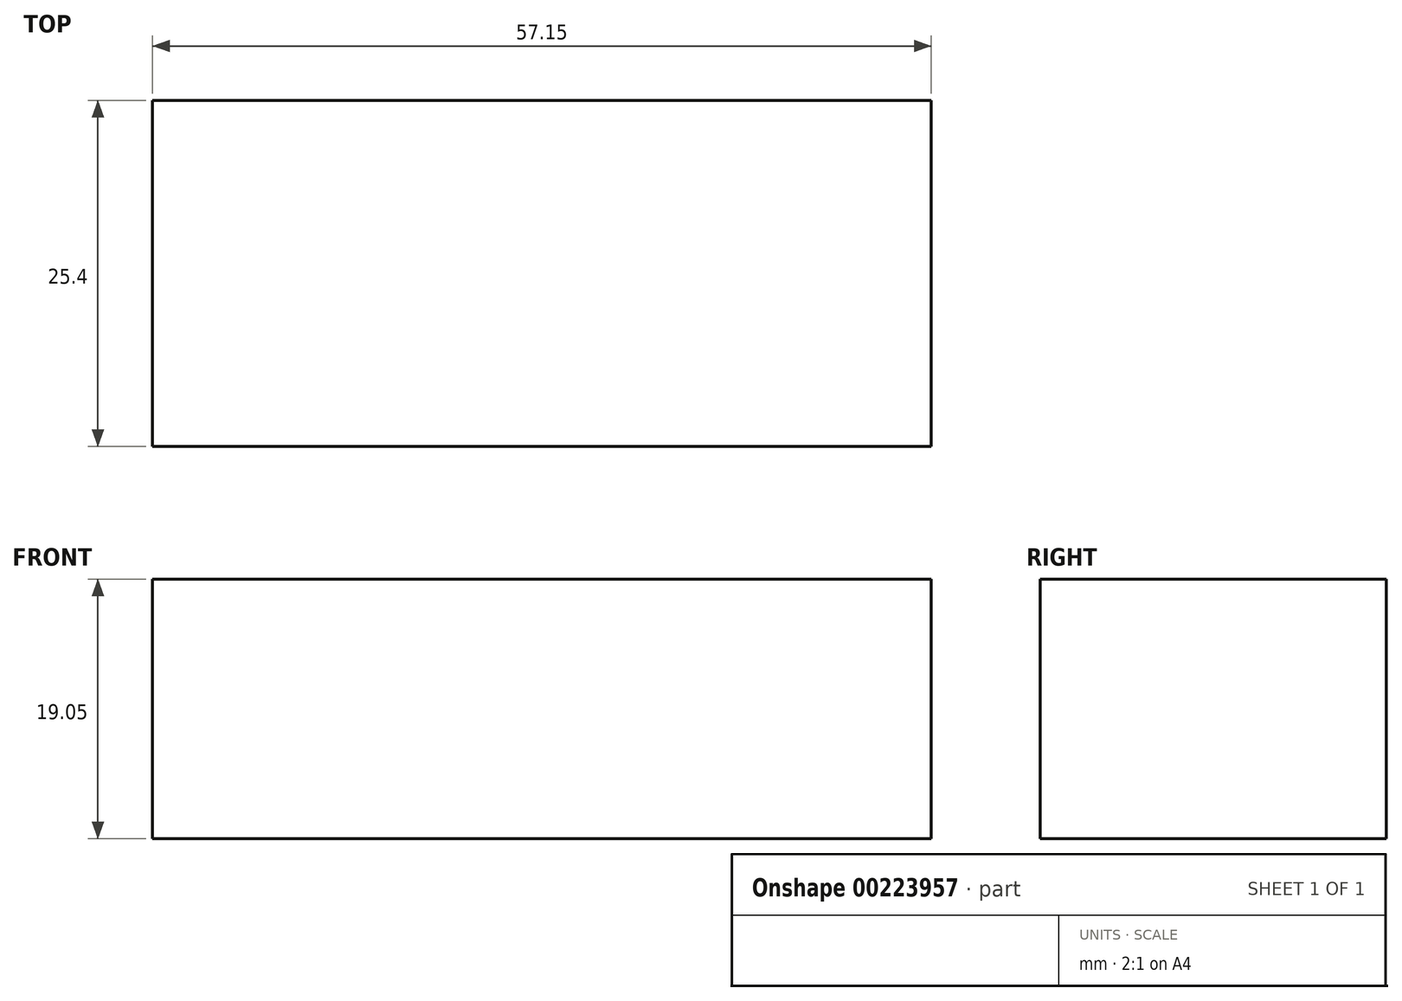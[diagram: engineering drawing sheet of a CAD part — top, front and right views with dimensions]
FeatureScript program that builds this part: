
annotation { "Feature Type Name" : "Feature", "Feature Type Description" : "" }
export const myFeature = defineFeature(function(context is Context, id is Id, definition is map)
    precondition{}
    {
        {
            var Q0;
            Q0=qCreatedBy(makeId("Front.planeOp"),FACE);
            var sketch = newSketch(context, id + "F0", { "sketchPlane" : qUnion([Q0])});
            skLineSegment(sketch, "E0.bottom", {"start": v(-0.52, 27.84) * mm, "end": v(-57.67, 27.84) * mm});
            skLineSegment(sketch, "E0.top", {"start": v(-0.52, 46.9) * mm, "end": v(-57.67, 46.9) * mm});
            skLineSegment(sketch, "E0.left", {"start": v(-0.52, 27.84) * mm, "end": v(-0.52, 46.9) * mm});
            skLineSegment(sketch, "E0.right", {"start": v(-57.67, 27.84) * mm, "end": v(-57.67, 46.9) * mm});
            skPoint(sketch, "E0.middle", {"position": v(-29.1, 37.37) * mm});
            skSolve(sketch);
        }
        {
            var Q0;
            Q0=makeQuery(id+"F0.imprint","IMPRINT",FACE,{"disambiguationData":[TD([[makeQuery(id+"F0.imprint","IMPRINT",EDGE,{"derivedFrom":sQuery(id+"F0.wireOp",EDGE,"E0.bottom")}),-1.0]])]});
            extrude(context, id + "F1", {"entities" : qUnion([Q0]), "endBound" : BoundingType.SYMMETRIC, "depth" : 25.4 * mm});
        }
    });
